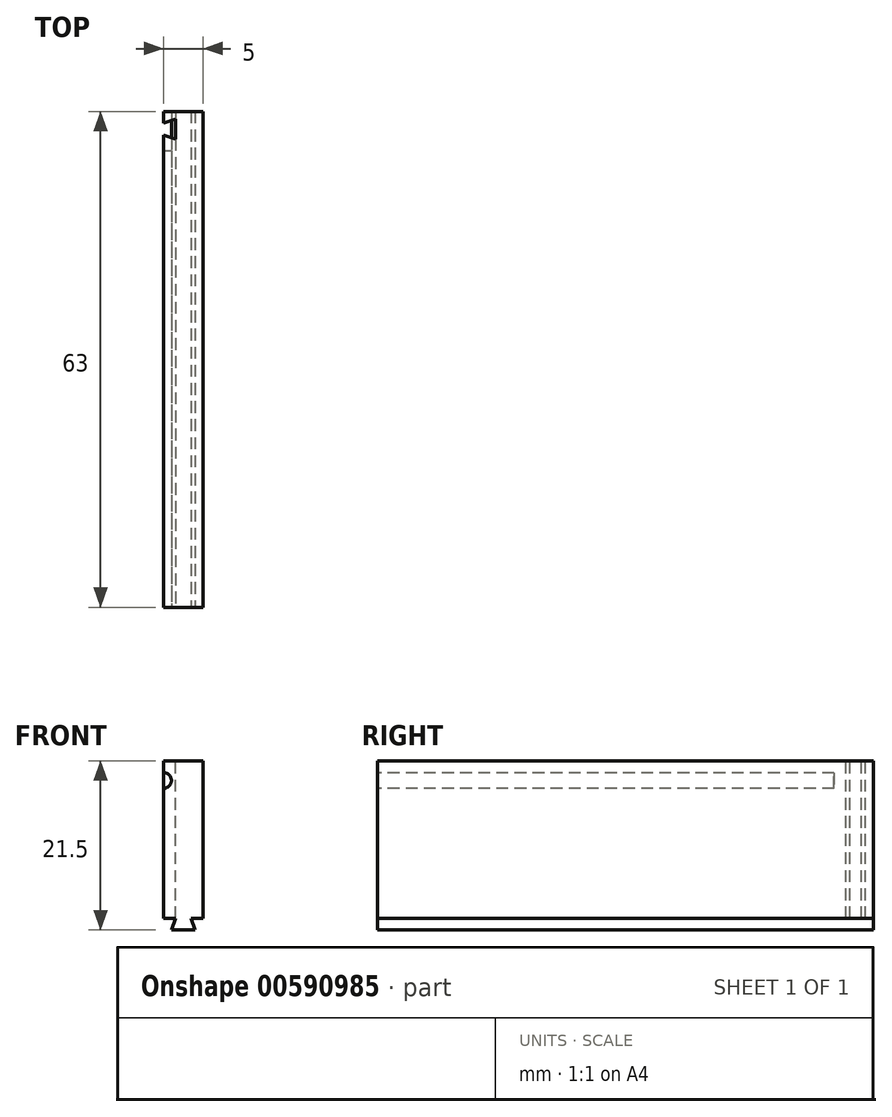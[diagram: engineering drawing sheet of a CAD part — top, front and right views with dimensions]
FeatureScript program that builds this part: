
annotation { "Feature Type Name" : "Feature", "Feature Type Description" : "" }
export const myFeature = defineFeature(function(context is Context, id is Id, definition is map)
    precondition{}
    {
        {
            var Q0;
            Q0=qCreatedBy(makeId("Right.planeOp"),FACE);
            var sketch = newSketch(context, id + "F0", { "sketchPlane" : qUnion([Q0])});
            skLineSegment(sketch, "E0.bottom", {"start": v(31.5, 10.75) * mm, "end": v(-31.5, 10.75) * mm});
            skLineSegment(sketch, "E0.top", {"start": v(31.5, -10.75) * mm, "end": v(-31.5, -10.75) * mm});
            skLineSegment(sketch, "E0.left", {"start": v(31.5, 10.75) * mm, "end": v(31.5, -10.75) * mm});
            skLineSegment(sketch, "E0.right", {"start": v(-31.5, 10.75) * mm, "end": v(-31.5, -10.75) * mm});
            skPoint(sketch, "E0.middle", {"position": v(0, 0) * mm});
            skSolve(sketch);
        }
        {
            var Q0;
            Q0=makeQuery(id+"F0.imprint","IMPRINT",FACE,{"disambiguationData":[TD([[makeQuery(id+"F0.imprint","IMPRINT",EDGE,{"derivedFrom":sQuery(id+"F0.wireOp",EDGE,"E0.bottom")}),1.0]])]});
            extrude(context, id + "F1", {"entities" : qUnion([Q0]), "depth" : 5 * mm, "offsetDistance" : 25 * mm});
        }
        {
            var Q0;
            Q0=makeQuery(id+"F1.opExtrude","SWEPT_FACE",FACE,{"disambiguationData":[OSD([sQuery(id+"F0.wireOp",EDGE,"E0.right")])]});
            var sketch = newSketch(context, id + "F2", { "sketchPlane" : qUnion([Q0])});
            skLineSegment(sketch, "E1", {"start": v(0, -9.25) * mm, "end": v(1.5, -9.25) * mm});
            skLineSegment(sketch, "E2", {"start": v(1.5, -9.25) * mm, "end": v(1, -10.75) * mm});
            skLineSegment(sketch, "E3", {"start": v(1, -10.75) * mm, "end": v(4, -10.75) * mm});
            skLineSegment(sketch, "E4", {"start": v(4, -10.75) * mm, "end": v(3.5, -9.25) * mm});
            skLineSegment(sketch, "E5", {"start": v(3.5, -9.25) * mm, "end": v(5, -9.25) * mm});
            skLineSegment(sketch, "E6", {"start": v(0, -9.25) * mm, "end": v(0, -10.75) * mm});
            skLineSegment(sketch, "E7", {"start": v(0, -10.75) * mm, "end": v(1, -10.75) * mm});
            skLineSegment(sketch, "E8", {"start": v(5, -9.25) * mm, "end": v(5, -10.75) * mm});
            skLineSegment(sketch, "E9", {"start": v(5, -10.75) * mm, "end": v(4, -10.75) * mm});
            skArc(sketch, "E10", {"start": v(0, 7.25) * mm, "mid": v(1, 8.25) * mm, "end": v(0, 9.25) * mm});
            skLineSegment(sketch, "E11", {"start": v(0, 9.25) * mm, "end": v(0, 7.25) * mm});
            skSolve(sketch);
        }
        {
            var Q0;
            Q0=makeQuery(id+"F2.imprint","IMPRINT",FACE,{"disambiguationData":[TD([[makeQuery(id+"F2.imprint","IMPRINT",EDGE,{"derivedFrom":sQuery(id+"F2.wireOp",EDGE,"E1")}),-1.0]])]});
            var Q1;
            Q1=makeQuery(id+"F2.imprint","IMPRINT",FACE,{"disambiguationData":[TD([[makeQuery(id+"F2.imprint","IMPRINT",EDGE,{"derivedFrom":sQuery(id+"F2.wireOp",EDGE,"E4")}),-1.0]])]});
            var Q2;
            {var subQ0=sQuery(id+"F2.wireOp",EDGE,"k4zaMBFN-SHmt-oLPD-lk5n-Gsra0QJAKv2b");Q2=makeQuery(id+"F2.imprint","IMPRINT",FACE,{"disambiguationData":[TD([[makeQuery(id+"F2.imprint","IMPRINT",EDGE,{"derivedFrom":subQ0}),1.0]])]});}
            extrude(context, id + "F3", {"entities" : qUnion([Q0, Q1, Q2]), "operationType" : NewBodyOperationType.REMOVE, "endBound" : BoundingType.THROUGH_ALL, "oppositeDirection" : true, "depth" : 129 * mm, "offsetDistance" : 25 * mm});
        }
        {
            var Q0;
            Q0=makeQuery(id+"F2.imprint","IMPRINT",FACE,{"disambiguationData":[TD([[makeQuery(id+"F2.imprint","IMPRINT",EDGE,{"derivedFrom":sQuery(id+"F2.wireOp",EDGE,"E10")}),1.0]])]});
            extrude(context, id + "F4", {"entities" : qUnion([Q0]), "operationType" : NewBodyOperationType.REMOVE, "oppositeDirection" : true, "depth" : 58 * mm, "offsetDistance" : 25 * mm});
        }
        {
            var Q0;
            Q0=makeQuery(id+"F1.opExtrude","SWEPT_FACE",FACE,{"disambiguationData":[OSD([sQuery(id+"F0.wireOp",EDGE,"E0.bottom")])]});
            var sketch = newSketch(context, id + "F5", { "sketchPlane" : qUnion([Q0])});
            skLineSegment(sketch, "E12", {"start": v(0, 30) * mm, "end": v(1.5, 30.5) * mm});
            skLineSegment(sketch, "E13", {"start": v(1.5, 30.5) * mm, "end": v(1.5, 28) * mm});
            skLineSegment(sketch, "E14", {"start": v(1.5, 28) * mm, "end": v(0, 28.5) * mm});
            skLineSegment(sketch, "E15", {"start": v(0, 28.5) * mm, "end": v(0, 30) * mm});
            skSolve(sketch);
        }
        {
            var Q0;
            Q0=makeQuery(id+"F5.imprint","IMPRINT",FACE,{"disambiguationData":[TD([[makeQuery(id+"F5.imprint","IMPRINT",EDGE,{"derivedFrom":sQuery(id+"F5.wireOp",EDGE,"E12")}),-1.0]])]});
            var Q1;
            Q1=makeQuery(id+"F3.boolean.opBoolean","COPY",FACE,{"derivedFrom":makeQuery(id+"F3.opExtrude","SWEPT_FACE",FACE,{"disambiguationData":[OSD([sQuery(id+"F2.wireOp",EDGE,"E1")])]})});
            extrude(context, id + "F6", {"entities" : qUnion([Q0]), "operationType" : NewBodyOperationType.REMOVE, "endBound" : BoundingType.UP_TO_SURFACE, "oppositeDirection" : true, "depth" : 25 * mm, "endBoundEntityFace" : qUnion([Q1]), "offsetDistance" : 25 * mm});
        }
    });
